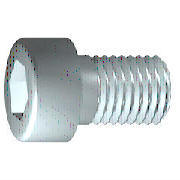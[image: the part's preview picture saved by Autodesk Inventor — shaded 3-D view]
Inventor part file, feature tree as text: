
AUTODESK INVENTOR PART (.ipt)
format: ipt  version: 2024 (Build 280153000, 153)  size: 193,536 bytes
history: native  units: mm (DEFAULTED — no unit token found)
features: fillet x2, sketch x2, extrude x1, thread x1, chamfer x1, plane x1
ambient origin geometry x7: Origin, YZ Plane, XY Plane, X Axis, Y Axis, Z Axis, Center Point
bodies: Solid1 (feature_tree), Body (feature_tree)
feature tree (8):
  extrude  "Slot"  Depth=3.0mm
  fillet  "Fillet1"  Radius=3.0mm
  thread  "Thread"  [1 undecoded]
  chamfer  "Chamfer1"  Distance=3.0mm
  plane  "Work Plane1"
  fillet  "Fillet2"  Radius=3.0mm
  sketch  "Sketch1"  dims[d1=6.75mm d2=0.306825mm d3=3.0mm d4=1.3mm]
  sketch  "Sketch2"  dims[d5=60.0deg d6=3.0mm d7=3.0mm d8=2.886751mm d9=5.5mm d10=90.0deg d11=10.0mm d12=0.0mm d13=6.75mm d14=0.0mm d15=0.306725mm d16=0.306725mm d17=0.3mm d19=0.0mm d26=8.0mm d27=45.0deg d28=0.0mm d29=0.0mm d30=0.1mm]
note: 1 required parameter value undecoded (feature->parameter linkage not recoverable at this tier; creation-order binding heuristic only, values carry confidence <= 0.55)
